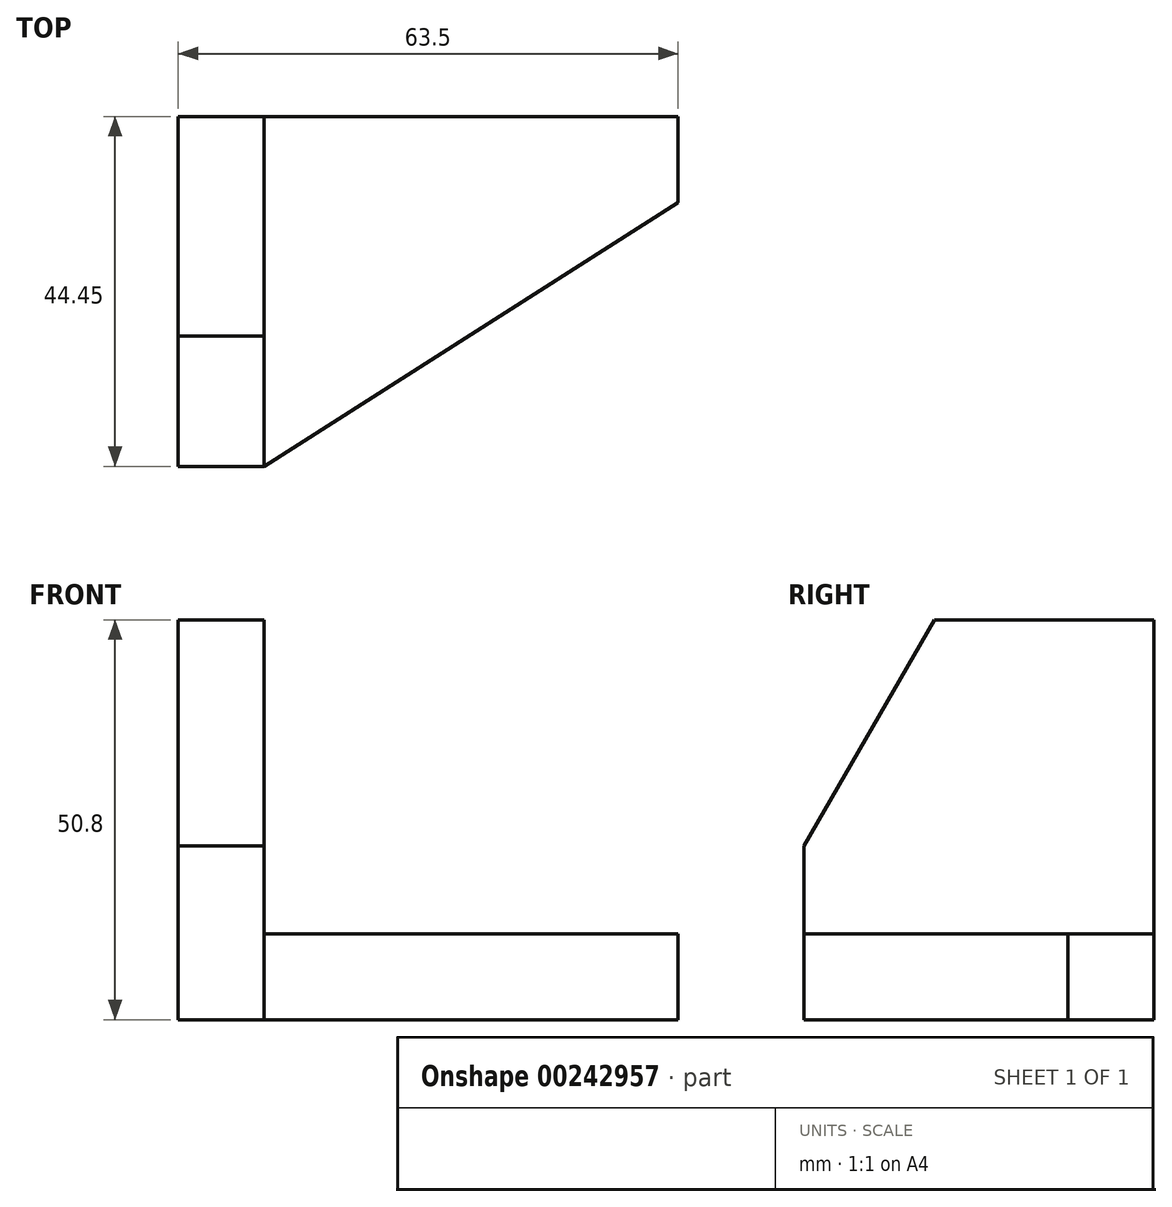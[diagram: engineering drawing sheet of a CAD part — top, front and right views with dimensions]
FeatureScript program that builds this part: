
annotation { "Feature Type Name" : "Feature", "Feature Type Description" : "" }
export const myFeature = defineFeature(function(context is Context, id is Id, definition is map)
    precondition{}
    {
        {
            var Q0;
            Q0=qCreatedBy(makeId("Front.planeOp"),FACE);
            var sketch = newSketch(context, id + "F0", { "sketchPlane" : qUnion([Q0])});
            skLineSegment(sketch, "E0.bottom", {"start": v(0, 0) * mm, "end": v(114.3, 0) * mm});
            skLineSegment(sketch, "E0.top", {"start": v(0, 60.2) * mm, "end": v(31.75, 60.2) * mm});
            skLineSegment(sketch, "E0.left", {"start": v(0, 0) * mm, "end": v(0, 60.2) * mm});
            skLineSegment(sketch, "E0.right", {"start": v(114.3, 0) * mm, "end": v(114.3, 38.08) * mm});
            skCircle(sketch, "E1", {"center": v(95.25, 19.05) * mm, "radius": 7.87 * mm});
            skLineSegment(sketch, "E2.top", {"start": v(0, 50.8) * mm, "end": v(10.92, 50.8) * mm});
            skLineSegment(sketch, "E2.left", {"start": v(0, 0) * mm, "end": v(0, 50.8) * mm});
            skLineSegment(sketch, "E2.right", {"start": v(10.92, 10.92) * mm, "end": v(10.92, 50.8) * mm});
            skLineSegment(sketch, "E3.top", {"start": v(10.92, 10.92) * mm, "end": v(63.5, 10.92) * mm});
            skLineSegment(sketch, "E3.right", {"start": v(63.5, 0) * mm, "end": v(63.5, 10.92) * mm});
            skLineSegment(sketch, "E4", {"start": v(31.75, 60.2) * mm, "end": v(114.3, 38.08) * mm});
            skSolve(sketch);
        }
        {
            var Q0;
            Q0=makeQuery(id+"F0.imprint","IMPRINT",FACE,{"disambiguationData":[TD([[makeQuery(id+"F0.imprint","IMPRINT",EDGE,{"derivedFrom":sQuery(id+"F0.wireOp",EDGE,"E0.bottom")}),1.0]])]});
            var Q1;
            Q1=makeQuery(id+"F0.imprint","IMPRINT",FACE,{"disambiguationData":[TD([[makeQuery(id+"F0.imprint","IMPRINT",EDGE,{"derivedFrom":sQuery(id+"F0.wireOp",EDGE,"E2.bottom")}),1.0]])]});
            extrude(context, id + "F1", {"entities" : qUnion([Q0, Q1]), "depth" : 10.92 * mm});
        }
        {
            var Q0;
            Q0=makeQuery(id+"F1.opExtrude","CAP_FACE",FACE,{"disambiguationData":[OSD([sQuery(id+"F0.wireOp",EDGE,"E0.bottom"),sQuery(id+"F0.wireOp",EDGE,"E0.top"),sQuery(id+"F0.wireOp",EDGE,"E0.left"),sQuery(id+"F0.wireOp",EDGE,"E0.right"),sQuery(id+"F0.wireOp",EDGE,"E1"),sQuery(id+"F0.wireOp",EDGE,"E2.bottom"),sQuery(id+"F0.wireOp",EDGE,"E2.left"),sQuery(id+"F0.wireOp",EDGE,"E3.bottom"),sQuery(id+"F0.wireOp",EDGE,"E4")])],"isStart":false});
            var sketch = newSketch(context, id + "F2", { "sketchPlane" : qUnion([Q0])});
            skLineSegment(sketch, "E5.bottom", {"start": v(0, 0) * mm, "end": v(10.92, 0) * mm});
            skLineSegment(sketch, "E5.top", {"start": v(0, 50.8) * mm, "end": v(10.92, 50.8) * mm});
            skLineSegment(sketch, "E5.left", {"start": v(0, 0) * mm, "end": v(0, 50.8) * mm});
            skLineSegment(sketch, "E5.right", {"start": v(10.92, 10.92) * mm, "end": v(10.92, 50.8) * mm});
            skLineSegment(sketch, "E6.bottom", {"start": v(0, 0) * mm, "end": v(63.5, 0) * mm});
            skLineSegment(sketch, "E6.top", {"start": v(10.92, 10.92) * mm, "end": v(63.5, 10.92) * mm});
            skLineSegment(sketch, "E6.left", {"start": v(0, 0) * mm, "end": v(0, 10.92) * mm});
            skLineSegment(sketch, "E6.right", {"start": v(63.5, 0) * mm, "end": v(63.5, 10.92) * mm});
            skSolve(sketch);
        }
        {
            var Q0;
            Q0=makeQuery(id+"F2.imprint","IMPRINT",FACE,{"disambiguationData":[TD([[makeQuery(id+"F2.imprint","IMPRINT",EDGE,{"derivedFrom":sQuery(id+"F2.wireOp",EDGE,"E5.top")}),-1.0]])]});
            extrude(context, id + "F3", {"entities" : qUnion([Q0]), "operationType" : NewBodyOperationType.ADD, "depth" : 33.53 * mm});
        }
        {
            var Q0;
            Q0=makeQuery(id+"F3.opExtrude","SWEPT_FACE",FACE,{"disambiguationData":[OSD([sQuery(id+"F2.wireOp",EDGE,"E6.top")])]});
            var sketch = newSketch(context, id + "F4", { "sketchPlane" : qUnion([Q0])});
            skLineSegment(sketch, "E7", {"start": v(10.92, -44.45) * mm, "end": v(63.5, -10.92) * mm});
            skSolve(sketch);
        }
        {
            var Q0;
            Q0=makeQuery(id+"F4.imprint","IMPRINT",FACE,{"disambiguationData":[TD([[makeQuery(id+"F4.imprint","IMPRINT",EDGE,{"derivedFrom":sQuery(id+"F4.wireOp",EDGE,"E7")}),-1.0]])]});
            extrude(context, id + "F5", {"entities" : qUnion([Q0]), "operationType" : NewBodyOperationType.REMOVE, "oppositeDirection" : true, "depth" : 25.4 * mm});
        }
        {
            var Q0;
            Q0=makeQuery(id+"F3.boolean.opBoolean","MERGE",FACE,{"derivedFrom":[makeQuery(id+"F1.opExtrude","SWEPT_FACE",FACE,{"disambiguationData":[OSD([sQuery(id+"F0.wireOp",EDGE,"E0.left"),sQuery(id+"F0.wireOp",EDGE,"E2.left")])]}),makeQuery(id+"F3.opExtrude","SWEPT_FACE",FACE,{"disambiguationData":[OSD([sQuery(id+"F2.wireOp",EDGE,"E5.left"),sQuery(id+"F2.wireOp",EDGE,"E6.left")])]})]});
            var sketch = newSketch(context, id + "F6", { "sketchPlane" : qUnion([Q0])});
            skLineSegment(sketch, "E8", {"start": v(44.45, 22.1) * mm, "end": v(27.88, 50.8) * mm});
            skSolve(sketch);
        }
        {
            var Q0;
            {var subQ0=sQuery(id+"F6.wireOp",EDGE,"E8");Q0=makeQuery(id+"F6.imprint","IMPRINT",FACE,{"disambiguationData":[TD([[makeQuery(id+"F6.imprint","IMPRINT",EDGE,{"derivedFrom":subQ0}),-1.0]])]});}
            extrude(context, id + "F7", {"entities" : qUnion([Q0]), "operationType" : NewBodyOperationType.REMOVE, "oppositeDirection" : true, "depth" : 25.4 * mm});
        }
    });
